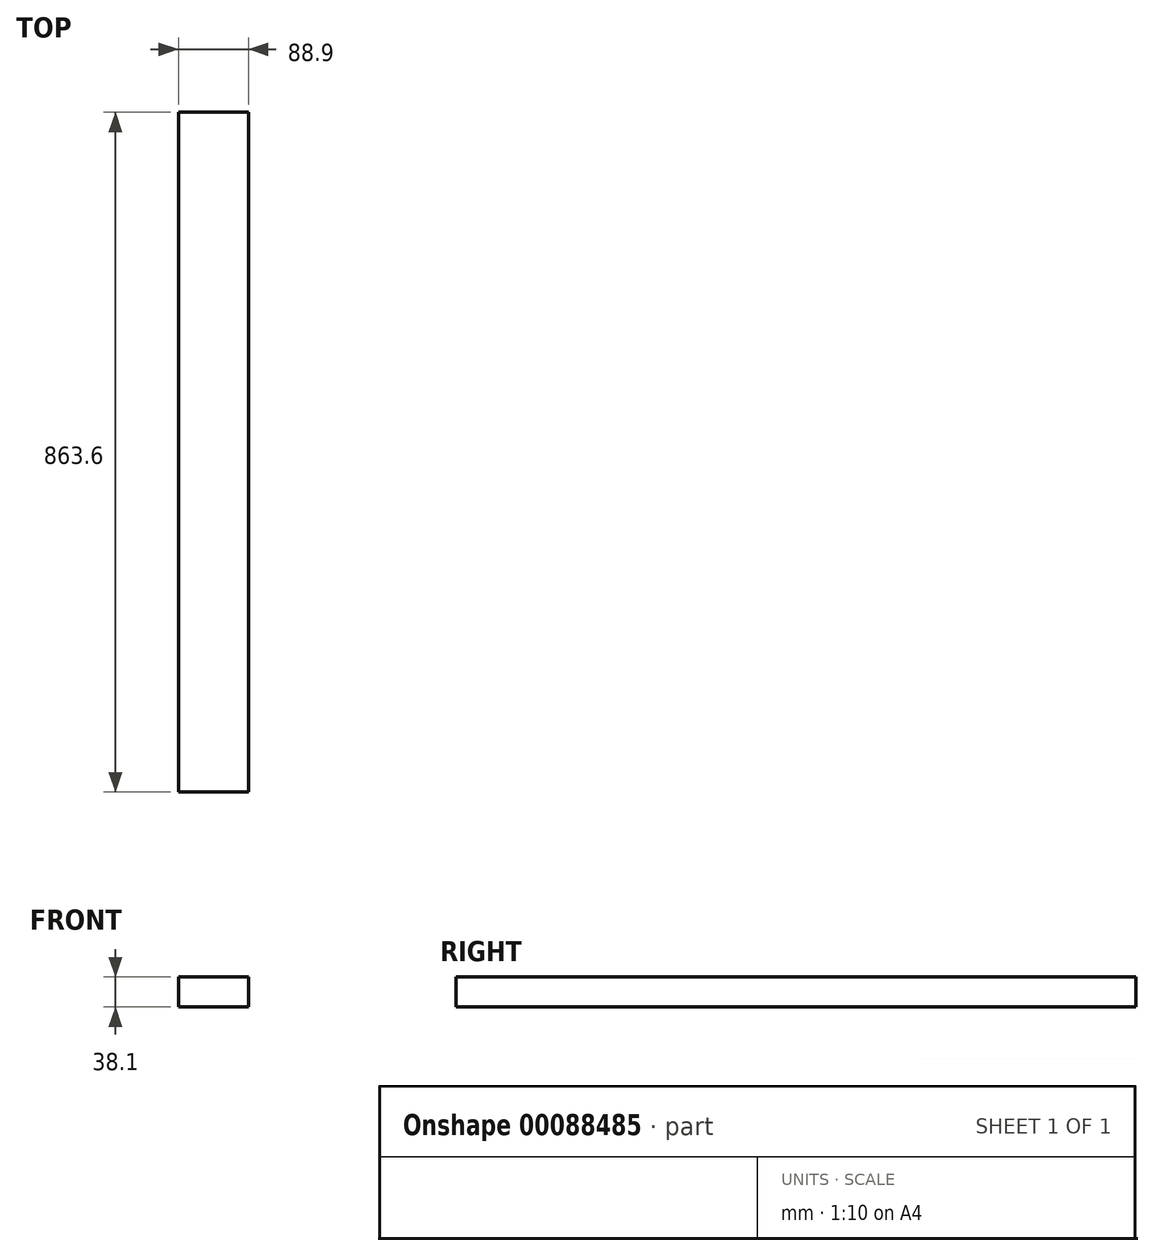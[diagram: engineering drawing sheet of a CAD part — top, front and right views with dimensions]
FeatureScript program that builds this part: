
annotation { "Feature Type Name" : "Feature", "Feature Type Description" : "" }
export const myFeature = defineFeature(function(context is Context, id is Id, definition is map)
    precondition{}
    {
        {
            var Q0;
            Q0=qCreatedBy(makeId("Front.planeOp"),FACE);
            var sketch = newSketch(context, id + "F0", { "sketchPlane" : qUnion([Q0])});
            skLineSegment(sketch, "E0.bottom", {"start": v(44.45, 19.05) * mm, "end": v(-44.45, 19.05) * mm});
            skLineSegment(sketch, "E0.top", {"start": v(44.45, -19.05) * mm, "end": v(-44.45, -19.05) * mm});
            skLineSegment(sketch, "E0.left", {"start": v(44.45, 19.05) * mm, "end": v(44.45, -19.05) * mm});
            skLineSegment(sketch, "E0.right", {"start": v(-44.45, 19.05) * mm, "end": v(-44.45, -19.05) * mm});
            skPoint(sketch, "E0.middle", {"position": v(0, 0) * mm});
            skSolve(sketch);
        }
        {
            var Q0;
            Q0=makeQuery(id+"F0.imprint","IMPRINT",FACE,{"disambiguationData":[TD([[makeQuery(id+"F0.imprint","IMPRINT",EDGE,{"derivedFrom":sQuery(id+"F0.wireOp",EDGE,"E0.bottom")}),1.0]])]});
            extrude(context, id + "F1", {"entities" : qUnion([Q0]), "endBound" : BoundingType.SYMMETRIC, "depth" : 863.6 * mm});
        }
    });
